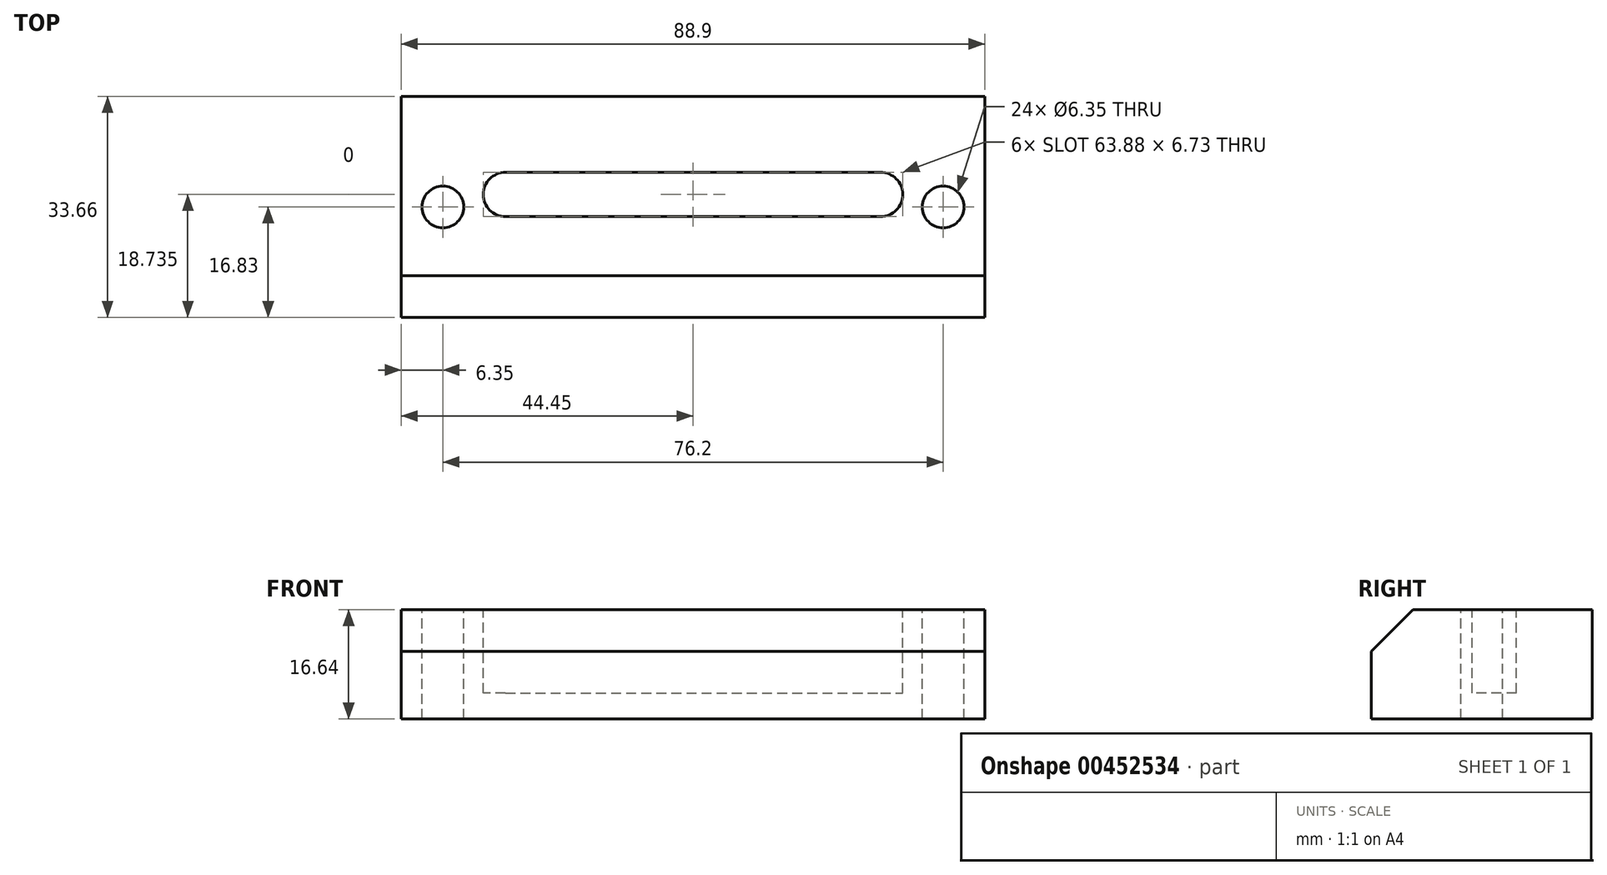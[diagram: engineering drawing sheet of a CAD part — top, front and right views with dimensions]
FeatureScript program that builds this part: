
annotation { "Feature Type Name" : "Feature", "Feature Type Description" : "" }
export const myFeature = defineFeature(function(context is Context, id is Id, definition is map)
    precondition{}
    {
        {
            var Q0;
            Q0=qCreatedBy(makeId("Top.planeOp"),FACE);
            var sketch = newSketch(context, id + "F0", { "sketchPlane" : qUnion([Q0])});
            skLineSegment(sketch, "E0.bottom", {"start": v(-44.45, 16.83) * mm, "end": v(44.45, 16.83) * mm});
            skLineSegment(sketch, "E0.top", {"start": v(-44.45, -16.83) * mm, "end": v(44.45, -16.83) * mm});
            skLineSegment(sketch, "E0.left", {"start": v(-44.45, 16.83) * mm, "end": v(-44.45, -16.83) * mm});
            skLineSegment(sketch, "E0.right", {"start": v(44.45, 16.83) * mm, "end": v(44.45, -16.83) * mm});
            skPoint(sketch, "E1", {"position": v(0, 16.83) * mm});
            skPoint(sketch, "E2", {"position": v(-44.45, 0) * mm});
            skCircle(sketch, "E3", {"center": v(-38.1, 0) * mm, "radius": 3.18 * mm});
            skCircle(sketch, "E4", {"center": v(38.1, 0) * mm, "radius": 3.18 * mm});
            skSolve(sketch);
        }
        {
            var Q0;
            Q0 = qSketchRegion(id + "F0", true);
            extrude(context, id + "F1", {"entities" : qUnion([Q0]), "oppositeDirection" : true, "depth" : 16.64 * mm});
        }
        {
            var Q0;
            Q0=makeQuery(id+"F1.opExtrude","CAP_FACE",FACE,{"disambiguationData":[OSD([sQuery(id+"F0.wireOp",EDGE,"E0.bottom"),sQuery(id+"F0.wireOp",EDGE,"E0.top"),sQuery(id+"F0.wireOp",EDGE,"E0.left"),sQuery(id+"F0.wireOp",EDGE,"E0.right"),sQuery(id+"F0.wireOp",EDGE,"E3"),sQuery(id+"F0.wireOp",EDGE,"E4")])],"isStart":true});
            var sketch = newSketch(context, id + "F2", { "sketchPlane" : qUnion([Q0])});
            skLineSegment(sketch, "E5.bottom", {"start": v(-28.58, 5.27) * mm, "end": v(28.58, 5.27) * mm});
            skLineSegment(sketch, "E5.top", {"start": v(-28.57, -1.46) * mm, "end": v(28.58, -1.46) * mm});
            skPoint(sketch, "E6", {"position": v(0, 5.27) * mm});
            skArc(sketch, "E7", {"start": v(-28.58, 5.27) * mm, "mid": v(-31.94, 1.9) * mm, "end": v(-28.57, -1.46) * mm});
            skArc(sketch, "E8", {"start": v(28.58, -1.46) * mm, "mid": v(31.94, 1.9) * mm, "end": v(28.58, 5.27) * mm});
            skSolve(sketch);
        }
        {
            var Q0;
            Q0 = qSketchRegion(id + "F2", true);
            extrude(context, id + "F3", {"entities" : qUnion([Q0]), "operationType" : NewBodyOperationType.REMOVE, "oppositeDirection" : true, "depth" : 12.7 * mm});
        }
        {
            var Q0;
            Q0=makeQuery(id+"F1.opExtrude","SWEPT_FACE",FACE,{"disambiguationData":[OSD([sQuery(id+"F0.wireOp",EDGE,"E0.left")])]});
            var sketch = newSketch(context, id + "F4", { "sketchPlane" : qUnion([Q0])});
            skLineSegment(sketch, "E9", {"start": v(10.48, 0) * mm, "end": v(16.83, -6.35) * mm});
            skLineSegment(sketch, "E10", {"start": v(10.48, 0) * mm, "end": v(16.83, 0) * mm});
            skLineSegment(sketch, "E11", {"start": v(16.83, 0) * mm, "end": v(16.83, -6.35) * mm});
            skSolve(sketch);
        }
        {
            var Q0;
            Q0 = qSketchRegion(id + "F4", true);
            extrude(context, id + "F5", {"entities" : qUnion([Q0]), "operationType" : NewBodyOperationType.REMOVE, "endBound" : BoundingType.THROUGH_ALL, "oppositeDirection" : true, "depth" : 25.4 * mm});
        }
    });
